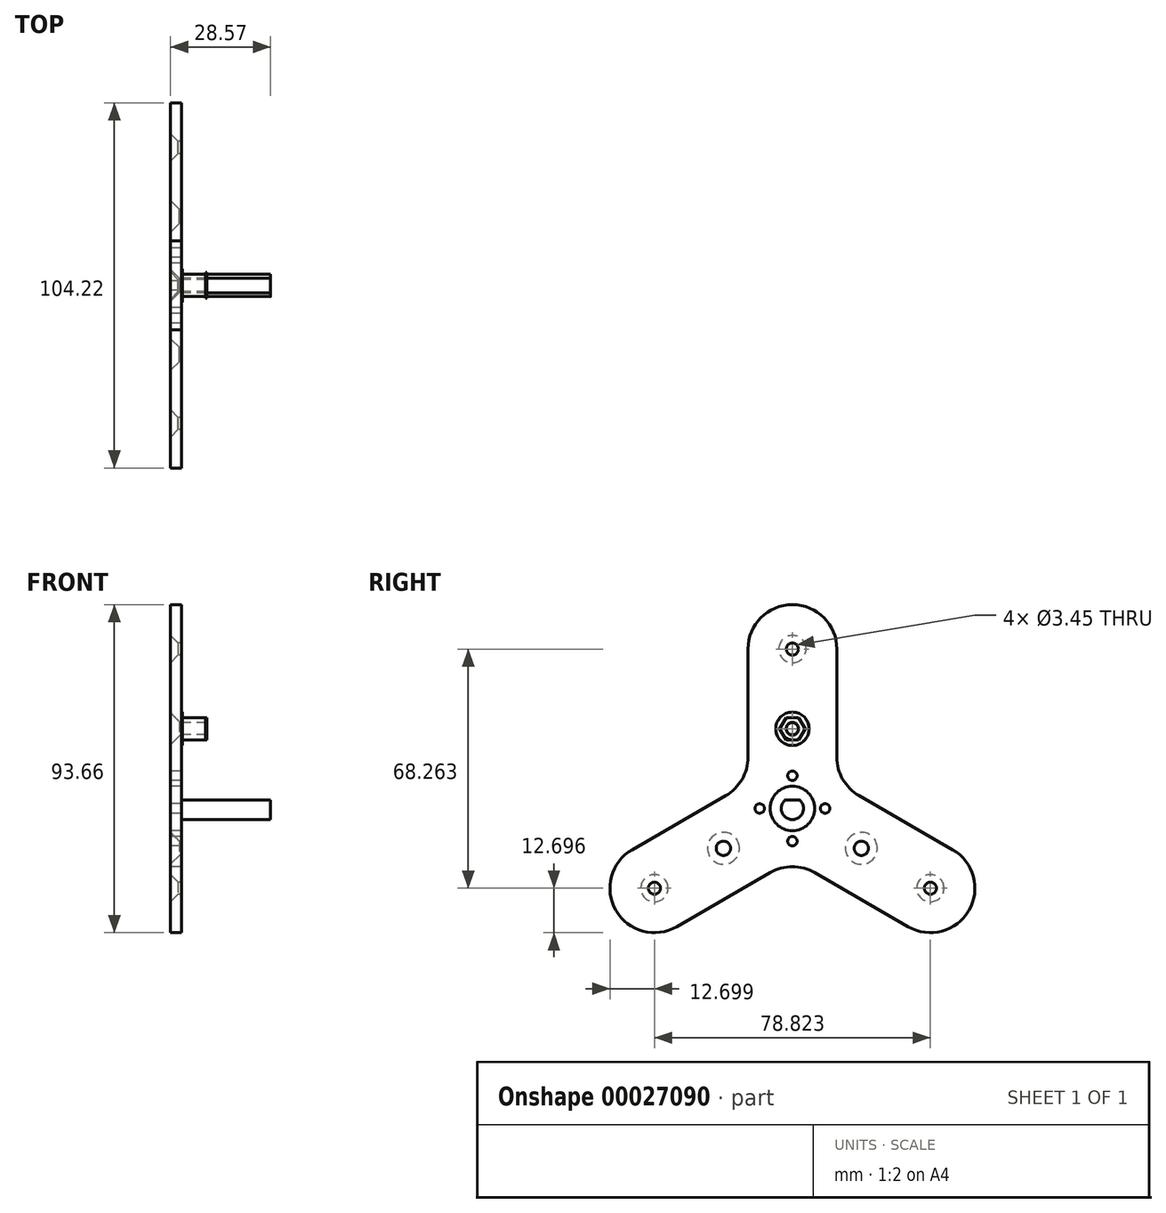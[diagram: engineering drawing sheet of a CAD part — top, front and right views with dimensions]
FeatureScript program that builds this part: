
annotation { "Feature Type Name" : "Feature", "Feature Type Description" : "" }
export const myFeature = defineFeature(function(context is Context, id is Id, definition is map)
    precondition{}
    {
        {
            var Q0;
            Q0=qCreatedBy(makeId("Right.planeOp"),FACE);
            var sketch = newSketch(context, id + "F0", { "sketchPlane" : qUnion([Q0])});
            skCircle(sketch, "E0.cCircle", {"center": v(0, 0) * mm, "radius": 45.5 * mm, "construction": true});
            skLineSegment(sketch, "E0.0", {"start": v(39.41, -22.75) * mm, "end": v(-39.41, -22.75) * mm, "construction": true});
            skLineSegment(sketch, "E0.2", {"start": v(0, 45.5) * mm, "end": v(39.41, -22.75) * mm, "construction": true});
            skCircle(sketch, "E1", {"center": v(-39.41, -22.75) * mm, "radius": 25.4 * mm});
            skCircle(sketch, "E2", {"center": v(39.41, -22.75) * mm, "radius": 25.4 * mm});
            skCircle(sketch, "E3", {"center": v(0, 45.5) * mm, "radius": 25.4 * mm});
            skCircle(sketch, "E4", {"center": v(0, 45.5) * mm, "radius": 14.82 * mm});
            skCircle(sketch, "E5", {"center": v(39.41, -22.75) * mm, "radius": 14.82 * mm});
            skCircle(sketch, "E6", {"center": v(-39.41, -22.75) * mm, "radius": 14.82 * mm});
            skCircle(sketch, "E7", {"center": v(0, 0) * mm, "radius": 14.82 * mm});
            skCircle(sketch, "E8", {"center": v(0, 22.75) * mm, "radius": 7.94 * mm});
            skCircle(sketch, "E9", {"center": v(19.7, -11.38) * mm, "radius": 7.94 * mm});
            skCircle(sketch, "E10", {"center": v(-19.7, -11.38) * mm, "radius": 7.94 * mm});
            skLineSegment(sketch, "E11", {"start": v(79.68, -48.15) * mm, "end": v(-88.84, -48.15) * mm, "construction": true});
            skCircle(sketch, "E12", {"center": v(0, 0) * mm, "radius": 12.7 * mm, "construction": true});
            skSolve(sketch);
        }
        {
            var Q0;
            Q0=qCreatedBy(makeId("Right.planeOp"),FACE);
            var sketch = newSketch(context, id + "F1", { "sketchPlane" : qUnion([Q0])});
            skPoint(sketch, "E13.0", {"position": v(0, 45.5) * mm});
            skPoint(sketch, "E13.1", {"position": v(39.41, -22.75) * mm});
            skPoint(sketch, "E13.2", {"position": v(-39.41, -22.75) * mm});
            skLineSegment(sketch, "E14", {"start": v(0, 45.5) * mm, "end": v(0, 0) * mm, "construction": true});
            skLineSegment(sketch, "E15", {"start": v(0, 0) * mm, "end": v(-39.41, -22.75) * mm, "construction": true});
            skLineSegment(sketch, "E16", {"start": v(0, 0) * mm, "end": v(39.41, -22.75) * mm, "construction": true});
            skArc(sketch, "E17.0.startCap", {"start": v(-6.35, -11) * mm, "mid": v(-11, 6.35) * mm, "end": v(6.35, 11) * mm, "construction": true});
            skArc(sketch, "E17.0.endCap", {"start": v(45.76, -11.76) * mm, "mid": v(50.4, -29.1) * mm, "end": v(33.06, -33.75) * mm});
            skLineSegment(sketch, "E17.0.left", {"start": v(19.05, 3.67) * mm, "end": v(45.76, -11.76) * mm});
            skLineSegment(sketch, "E17.0.right", {"start": v(6.35, -18.33) * mm, "end": v(33.06, -33.75) * mm});
            skArc(sketch, "E17.1.startCap", {"start": v(-6.35, 11) * mm, "mid": v(11, 6.35) * mm, "end": v(6.35, -11) * mm, "construction": true});
            skArc(sketch, "E17.1.endCap", {"start": v(-33.06, -33.75) * mm, "mid": v(-50.4, -29.1) * mm, "end": v(-45.76, -11.76) * mm});
            skLineSegment(sketch, "E17.1.left", {"start": v(-6.35, -18.33) * mm, "end": v(-33.06, -33.75) * mm});
            skLineSegment(sketch, "E17.1.right", {"start": v(-19.05, 3.67) * mm, "end": v(-45.76, -11.76) * mm});
            skArc(sketch, "E17.2.startCap", {"start": v(-12.7, 45.5) * mm, "mid": v(0, 58.2) * mm, "end": v(12.7, 45.5) * mm});
            skArc(sketch, "E17.2.endCap", {"start": v(12.7, 0) * mm, "mid": v(0, -12.7) * mm, "end": v(-12.7, 0) * mm, "construction": true});
            skLineSegment(sketch, "E17.2.left", {"start": v(12.7, 45.5) * mm, "end": v(12.7, 14.66) * mm});
            skLineSegment(sketch, "E17.2.right", {"start": v(-12.7, 45.5) * mm, "end": v(-12.7, 14.66) * mm});
            skPoint(sketch, "E18.0", {"position": v(0, 22.75) * mm});
            skPoint(sketch, "E18.1", {"position": v(19.7, -11.38) * mm});
            skPoint(sketch, "E18.2", {"position": v(-19.7, -11.38) * mm});
            skPoint(sketch, "E19.visualSharp", {"position": v(-12.7, 7.33) * mm});
            skArc(sketch, "E19.filletArc", {"start": v(-19.05, 3.67) * mm, "mid": v(-14.4, 8.31) * mm, "end": v(-12.7, 14.66) * mm});
            skPoint(sketch, "E20.visualSharp", {"position": v(0, -14.66) * mm});
            skArc(sketch, "E20.filletArc", {"start": v(6.35, -18.33) * mm, "mid": v(0, -16.63) * mm, "end": v(-6.35, -18.33) * mm});
            skPoint(sketch, "E21.visualSharp", {"position": v(12.7, 7.33) * mm});
            skArc(sketch, "E21.filletArc", {"start": v(12.7, 14.66) * mm, "mid": v(14.4, 8.31) * mm, "end": v(19.05, 3.67) * mm});
            skSolve(sketch);
        }
        {
            var Q0;
            Q0 = qSketchRegion(id + "F1", true);
            extrude(context, id + "F2", {"entities" : qUnion([Q0]), "depth" : 3.17 * mm});
        }
        {
            var Q0;
            Q0=sQuery(id+"F1.wireOp",VERTEX,"E13.0");
            var Q1;
            Q1=sQuery(id+"F1.wireOp",VERTEX,"E13.1");
            var Q2;
            Q2=sQuery(id+"F1.wireOp",VERTEX,"E13.2");
            var Q3;
            Q3=makeQuery(id+"F2.opExtrude","SWEPT_BODY",BODY,{"disambiguationData":[OSD([sQuery(id+"F1.wireOp",EDGE,"E17.0.endCap"),sQuery(id+"F1.wireOp",EDGE,"E17.0.left"),sQuery(id+"F1.wireOp",EDGE,"E17.0.right"),sQuery(id+"F1.wireOp",EDGE,"E17.1.endCap"),sQuery(id+"F1.wireOp",EDGE,"E17.1.left"),sQuery(id+"F1.wireOp",EDGE,"E17.1.right"),sQuery(id+"F1.wireOp",EDGE,"E17.2.startCap"),sQuery(id+"F1.wireOp",EDGE,"E17.2.left"),sQuery(id+"F1.wireOp",EDGE,"E17.2.right"),sQuery(id+"F1.wireOp",EDGE,"E19.filletArc"),sQuery(id+"F1.wireOp",EDGE,"E20.filletArc"),sQuery(id+"F1.wireOp",EDGE,"E21.filletArc")])]});
            hole(context, id + "F3", {"style" : HoleStyle.C_SINK, "holeDiameter" : 3.45 * mm, "cSinkDiameter" : 7.8 * mm, "endStyle" : HoleEndStyle.THROUGH, "oppositeDirection" : true, "locations" : qUnion([Q0, Q1, Q2]), "scope" : qUnion([Q3]), "cSinkAngle" : 90 * degree});
        }
        {
            var Q0;
            Q0=sQuery(id+"F1.wireOp",VERTEX,"E18.0");
            var Q1;
            Q1=sQuery(id+"F1.wireOp",VERTEX,"E18.2");
            var Q2;
            Q2=sQuery(id+"F1.wireOp",VERTEX,"E18.1");
            var Q3;
            Q3=makeQuery(id+"F2.opExtrude","SWEPT_BODY",BODY,{"disambiguationData":[OSD([sQuery(id+"F1.wireOp",EDGE,"E17.0.endCap"),sQuery(id+"F1.wireOp",EDGE,"E17.0.left"),sQuery(id+"F1.wireOp",EDGE,"E17.0.right"),sQuery(id+"F1.wireOp",EDGE,"E17.1.endCap"),sQuery(id+"F1.wireOp",EDGE,"E17.1.left"),sQuery(id+"F1.wireOp",EDGE,"E17.1.right"),sQuery(id+"F1.wireOp",EDGE,"E17.2.startCap"),sQuery(id+"F1.wireOp",EDGE,"E17.2.left"),sQuery(id+"F1.wireOp",EDGE,"E17.2.right"),sQuery(id+"F1.wireOp",EDGE,"E19.filletArc"),sQuery(id+"F1.wireOp",EDGE,"E20.filletArc"),sQuery(id+"F1.wireOp",EDGE,"E21.filletArc")])]});
            hole(context, id + "F4", {"style" : HoleStyle.SIMPLE, "holeDiameter" : 4.1 * mm, "endStyle" : HoleEndStyle.THROUGH, "oppositeDirection" : true, "locations" : qUnion([Q0, Q1, Q2]), "scope" : qUnion([Q3])});
        }
        {
            var Q0;
            Q0=makeQuery(id+"F2.opExtrude","CAP_FACE",FACE,{"disambiguationData":[OSD([sQuery(id+"F1.wireOp",EDGE,"E17.0.endCap"),sQuery(id+"F1.wireOp",EDGE,"E17.0.left"),sQuery(id+"F1.wireOp",EDGE,"E17.0.right"),sQuery(id+"F1.wireOp",EDGE,"E17.1.endCap"),sQuery(id+"F1.wireOp",EDGE,"E17.1.left"),sQuery(id+"F1.wireOp",EDGE,"E17.1.right"),sQuery(id+"F1.wireOp",EDGE,"E17.2.startCap"),sQuery(id+"F1.wireOp",EDGE,"E17.2.left"),sQuery(id+"F1.wireOp",EDGE,"E17.2.right"),sQuery(id+"F1.wireOp",EDGE,"E19.filletArc"),sQuery(id+"F1.wireOp",EDGE,"E20.filletArc"),sQuery(id+"F1.wireOp",EDGE,"E21.filletArc")])],"isStart":false});
            var sketch = newSketch(context, id + "F5", { "sketchPlane" : qUnion([Q0])});
            skCircle(sketch, "E22.cCircle", {"center": v(0, 22.75) * mm, "radius": 3.18 * mm});
            skLineSegment(sketch, "E22.0", {"start": v(3.67, 22.75) * mm, "end": v(1.83, 19.58) * mm});
            skLineSegment(sketch, "E22.1", {"start": v(1.83, 19.58) * mm, "end": v(-1.83, 19.58) * mm});
            skLineSegment(sketch, "E22.2", {"start": v(-1.83, 19.58) * mm, "end": v(-3.67, 22.75) * mm});
            skLineSegment(sketch, "E22.3", {"start": v(-3.67, 22.75) * mm, "end": v(-1.83, 25.93) * mm});
            skLineSegment(sketch, "E22.4", {"start": v(-1.83, 25.93) * mm, "end": v(1.83, 25.93) * mm});
            skLineSegment(sketch, "E22.5", {"start": v(1.83, 25.93) * mm, "end": v(3.67, 22.75) * mm});
            skPoint(sketch, "E22.0.midPoint", {"position": v(2.75, 21.17) * mm});
            skCircle(sketch, "E23", {"center": v(0, 22.75) * mm, "radius": 1.73 * mm});
            skCircle(sketch, "E24", {"center": v(0, 22.75) * mm, "radius": 4.76 * mm});
            skSolve(sketch);
        }
        {
            var Q0;
            {var subQ0=sQuery(id+"F5.wireOp",EDGE,"E22.cCircle");var subQ6=makeQuery(id+"F5.imprint","INTERSECT",VERTEX,{"derivedFrom":[subQ0,sQuery(id+"F5.wireOp",EDGE,"E22.4")]});Q0=makeQuery(id+"F5.imprint","IMPRINT",FACE,{"disambiguationData":[TD([[makeQuery(id+"F5.imprint","IMPRINT",EDGE,{"disambiguationData":[TD([[subQ6,1.0]])],"derivedFrom":subQ0}),1.0]])]});}
            var Q1;
            {var subQ0=sQuery(id+"F5.wireOp",EDGE,"E22.2");var subQ1=sQuery(id+"F5.wireOp",EDGE,"E22.cCircle");var subQ2=makeQuery(id+"F5.imprint","INTERSECT",VERTEX,{"derivedFrom":[subQ1,subQ0]});Q1=makeQuery(id+"F5.imprint","IMPRINT",FACE,{"disambiguationData":[TD([[makeQuery(id+"F5.imprint","IMPRINT",EDGE,{"disambiguationData":[TD([[subQ2,-1.0]])],"derivedFrom":subQ1}),-1.0]])]});}
            var Q2;
            {var subQ0=sQuery(id+"F5.wireOp",EDGE,"E22.3");var subQ1=sQuery(id+"F5.wireOp",EDGE,"E22.cCircle");var subQ2=makeQuery(id+"F5.imprint","INTERSECT",VERTEX,{"derivedFrom":[subQ1,subQ0]});Q2=makeQuery(id+"F5.imprint","IMPRINT",FACE,{"disambiguationData":[TD([[makeQuery(id+"F5.imprint","IMPRINT",EDGE,{"disambiguationData":[TD([[subQ2,-1.0]])],"derivedFrom":subQ1}),-1.0]])]});}
            var Q3;
            {var subQ0=sQuery(id+"F5.wireOp",EDGE,"E22.4");var subQ1=sQuery(id+"F5.wireOp",EDGE,"E22.cCircle");var subQ2=makeQuery(id+"F5.imprint","INTERSECT",VERTEX,{"derivedFrom":[subQ1,subQ0]});Q3=makeQuery(id+"F5.imprint","IMPRINT",FACE,{"disambiguationData":[TD([[makeQuery(id+"F5.imprint","IMPRINT",EDGE,{"disambiguationData":[TD([[subQ2,-1.0]])],"derivedFrom":subQ1}),-1.0]])]});}
            var Q4;
            {var subQ1=sQuery(id+"F5.wireOp",EDGE,"E22.cCircle");var subQ3=sQuery(id+"F5.wireOp",EDGE,"E22.4");var subQ5=makeQuery(id+"F5.imprint","INTERSECT",VERTEX,{"derivedFrom":[subQ1,subQ3]});Q4=makeQuery(id+"F5.imprint","IMPRINT",FACE,{"disambiguationData":[TD([[makeQuery(id+"F5.imprint","IMPRINT",EDGE,{"disambiguationData":[TD([[subQ5,1.0]])],"derivedFrom":subQ1}),-1.0]])]});}
            var Q5;
            {var subQ0=sQuery(id+"F5.wireOp",EDGE,"E22.5");var subQ1=sQuery(id+"F5.wireOp",EDGE,"E22.cCircle");var subQ2=makeQuery(id+"F5.imprint","INTERSECT",VERTEX,{"derivedFrom":[subQ1,subQ0]});Q5=makeQuery(id+"F5.imprint","IMPRINT",FACE,{"disambiguationData":[TD([[makeQuery(id+"F5.imprint","IMPRINT",EDGE,{"disambiguationData":[TD([[subQ2,1.0]])],"derivedFrom":subQ1}),-1.0]])]});}
            var Q6;
            {var subQ0=sQuery(id+"F5.wireOp",EDGE,"E22.1");var subQ1=sQuery(id+"F5.wireOp",EDGE,"E22.cCircle");var subQ2=makeQuery(id+"F5.imprint","INTERSECT",VERTEX,{"derivedFrom":[subQ1,subQ0]});Q6=makeQuery(id+"F5.imprint","IMPRINT",FACE,{"disambiguationData":[TD([[makeQuery(id+"F5.imprint","IMPRINT",EDGE,{"disambiguationData":[TD([[subQ2,-1.0]])],"derivedFrom":subQ1}),-1.0]])]});}
            var Q7;
            Q7=makeQuery(id+"F5.imprint","IMPRINT",FACE,{"disambiguationData":[TD([[makeQuery(id+"F5.imprint","IMPRINT",EDGE,{"derivedFrom":sQuery(id+"F5.wireOp",EDGE,"E23")}),-1.0]])]});
            extrude(context, id + "F6", {"entities" : qUnion([Q0, Q1, Q2, Q3, Q4, Q5, Q6, Q7]), "depth" : 7.24 * mm});
        }
        {
            var Q0;
            {var subQ1=sQuery(id+"F5.wireOp",EDGE,"E22.cCircle");var subQ3=sQuery(id+"F5.wireOp",EDGE,"E22.4");var subQ5=makeQuery(id+"F5.imprint","INTERSECT",VERTEX,{"derivedFrom":[subQ1,subQ3]});Q0=makeQuery(id+"F5.imprint","IMPRINT",FACE,{"disambiguationData":[TD([[makeQuery(id+"F5.imprint","IMPRINT",EDGE,{"disambiguationData":[TD([[subQ5,1.0]])],"derivedFrom":subQ1}),-1.0]])]});}
            var Q1;
            {var subQ0=sQuery(id+"F5.wireOp",EDGE,"E22.5");var subQ1=sQuery(id+"F5.wireOp",EDGE,"E22.cCircle");var subQ2=makeQuery(id+"F5.imprint","INTERSECT",VERTEX,{"derivedFrom":[subQ1,subQ0]});Q1=makeQuery(id+"F5.imprint","IMPRINT",FACE,{"disambiguationData":[TD([[makeQuery(id+"F5.imprint","IMPRINT",EDGE,{"disambiguationData":[TD([[subQ2,1.0]])],"derivedFrom":subQ1}),-1.0]])]});}
            var Q2;
            {var subQ0=sQuery(id+"F5.wireOp",EDGE,"E22.1");var subQ1=sQuery(id+"F5.wireOp",EDGE,"E22.cCircle");var subQ2=makeQuery(id+"F5.imprint","INTERSECT",VERTEX,{"derivedFrom":[subQ1,subQ0]});Q2=makeQuery(id+"F5.imprint","IMPRINT",FACE,{"disambiguationData":[TD([[makeQuery(id+"F5.imprint","IMPRINT",EDGE,{"disambiguationData":[TD([[subQ2,-1.0]])],"derivedFrom":subQ1}),-1.0]])]});}
            var Q3;
            {var subQ0=sQuery(id+"F5.wireOp",EDGE,"E22.3");var subQ1=sQuery(id+"F5.wireOp",EDGE,"E22.cCircle");var subQ2=makeQuery(id+"F5.imprint","INTERSECT",VERTEX,{"derivedFrom":[subQ1,subQ0]});Q3=makeQuery(id+"F5.imprint","IMPRINT",FACE,{"disambiguationData":[TD([[makeQuery(id+"F5.imprint","IMPRINT",EDGE,{"disambiguationData":[TD([[subQ2,-1.0]])],"derivedFrom":subQ1}),-1.0]])]});}
            var Q4;
            {var subQ0=sQuery(id+"F5.wireOp",EDGE,"E22.4");var subQ1=sQuery(id+"F5.wireOp",EDGE,"E22.cCircle");var subQ2=makeQuery(id+"F5.imprint","INTERSECT",VERTEX,{"derivedFrom":[subQ1,subQ0]});Q4=makeQuery(id+"F5.imprint","IMPRINT",FACE,{"disambiguationData":[TD([[makeQuery(id+"F5.imprint","IMPRINT",EDGE,{"disambiguationData":[TD([[subQ2,-1.0]])],"derivedFrom":subQ1}),-1.0]])]});}
            var Q5;
            {var subQ0=sQuery(id+"F5.wireOp",EDGE,"E22.2");var subQ1=sQuery(id+"F5.wireOp",EDGE,"E22.cCircle");var subQ2=makeQuery(id+"F5.imprint","INTERSECT",VERTEX,{"derivedFrom":[subQ1,subQ0]});Q5=makeQuery(id+"F5.imprint","IMPRINT",FACE,{"disambiguationData":[TD([[makeQuery(id+"F5.imprint","IMPRINT",EDGE,{"disambiguationData":[TD([[subQ2,-1.0]])],"derivedFrom":subQ1}),-1.0]])]});}
            extrude(context, id + "F7", {"entities" : qUnion([Q0, Q1, Q2, Q3, Q4, Q5]), "operationType" : NewBodyOperationType.REMOVE, "depth" : 6.8 * mm});
        }
        {
            var Q0;
            Q0=makeQuery(id+"F5.imprint","IMPRINT",FACE,{"disambiguationData":[TD([[makeQuery(id+"F5.imprint","IMPRINT",EDGE,{"derivedFrom":sQuery(id+"F5.wireOp",EDGE,"E24")}),1.0]])]});
            var Q1;
            {var subQ0=sQuery(id+"F5.wireOp",EDGE,"E22.4");var subQ1=sQuery(id+"F5.wireOp",EDGE,"E22.cCircle");var subQ2=makeQuery(id+"F5.imprint","INTERSECT",VERTEX,{"derivedFrom":[subQ1,subQ0]});Q1=makeQuery(id+"F5.imprint","IMPRINT",FACE,{"disambiguationData":[TD([[makeQuery(id+"F5.imprint","IMPRINT",EDGE,{"disambiguationData":[TD([[subQ2,-1.0]])],"derivedFrom":subQ1}),-1.0]])]});}
            var Q2;
            {var subQ0=sQuery(id+"F5.wireOp",EDGE,"E22.3");var subQ1=sQuery(id+"F5.wireOp",EDGE,"E22.cCircle");var subQ2=makeQuery(id+"F5.imprint","INTERSECT",VERTEX,{"derivedFrom":[subQ1,subQ0]});Q2=makeQuery(id+"F5.imprint","IMPRINT",FACE,{"disambiguationData":[TD([[makeQuery(id+"F5.imprint","IMPRINT",EDGE,{"disambiguationData":[TD([[subQ2,-1.0]])],"derivedFrom":subQ1}),-1.0]])]});}
            var Q3;
            {var subQ0=sQuery(id+"F5.wireOp",EDGE,"E22.2");var subQ1=sQuery(id+"F5.wireOp",EDGE,"E22.cCircle");var subQ2=makeQuery(id+"F5.imprint","INTERSECT",VERTEX,{"derivedFrom":[subQ1,subQ0]});Q3=makeQuery(id+"F5.imprint","IMPRINT",FACE,{"disambiguationData":[TD([[makeQuery(id+"F5.imprint","IMPRINT",EDGE,{"disambiguationData":[TD([[subQ2,-1.0]])],"derivedFrom":subQ1}),-1.0]])]});}
            var Q4;
            {var subQ0=sQuery(id+"F5.wireOp",EDGE,"E22.1");var subQ1=sQuery(id+"F5.wireOp",EDGE,"E22.cCircle");var subQ2=makeQuery(id+"F5.imprint","INTERSECT",VERTEX,{"derivedFrom":[subQ1,subQ0]});Q4=makeQuery(id+"F5.imprint","IMPRINT",FACE,{"disambiguationData":[TD([[makeQuery(id+"F5.imprint","IMPRINT",EDGE,{"disambiguationData":[TD([[subQ2,-1.0]])],"derivedFrom":subQ1}),-1.0]])]});}
            var Q5;
            {var subQ0=sQuery(id+"F5.wireOp",EDGE,"E22.5");var subQ1=sQuery(id+"F5.wireOp",EDGE,"E22.cCircle");var subQ2=makeQuery(id+"F5.imprint","INTERSECT",VERTEX,{"derivedFrom":[subQ1,subQ0]});Q5=makeQuery(id+"F5.imprint","IMPRINT",FACE,{"disambiguationData":[TD([[makeQuery(id+"F5.imprint","IMPRINT",EDGE,{"disambiguationData":[TD([[subQ2,1.0]])],"derivedFrom":subQ1}),-1.0]])]});}
            var Q6;
            {var subQ1=sQuery(id+"F5.wireOp",EDGE,"E22.cCircle");var subQ3=sQuery(id+"F5.wireOp",EDGE,"E22.4");var subQ5=makeQuery(id+"F5.imprint","INTERSECT",VERTEX,{"derivedFrom":[subQ1,subQ3]});Q6=makeQuery(id+"F5.imprint","IMPRINT",FACE,{"disambiguationData":[TD([[makeQuery(id+"F5.imprint","IMPRINT",EDGE,{"disambiguationData":[TD([[subQ5,1.0]])],"derivedFrom":subQ1}),-1.0]])]});}
            extrude(context, id + "F8", {"entities" : qUnion([Q0, Q1, Q2, Q3, Q4, Q5, Q6]), "depth" : 0.25 * mm});
        }
        {
            var Q0;
            Q0=sQuery(id+"F0.wireOp",VERTEX,"E8.center");
            var Q1;
            Q1=sQuery(id+"F0.wireOp",VERTEX,"E9.center");
            var Q2;
            Q2=sQuery(id+"F0.wireOp",VERTEX,"E10.center");
            var Q3;
            Q3=makeQuery(id+"F2.opExtrude","SWEPT_BODY",BODY,{"disambiguationData":[OSD([sQuery(id+"F1.wireOp",EDGE,"E17.0.endCap"),sQuery(id+"F1.wireOp",EDGE,"E17.0.left"),sQuery(id+"F1.wireOp",EDGE,"E17.0.right"),sQuery(id+"F1.wireOp",EDGE,"E17.1.endCap"),sQuery(id+"F1.wireOp",EDGE,"E17.1.left"),sQuery(id+"F1.wireOp",EDGE,"E17.1.right"),sQuery(id+"F1.wireOp",EDGE,"E17.2.startCap"),sQuery(id+"F1.wireOp",EDGE,"E17.2.left"),sQuery(id+"F1.wireOp",EDGE,"E17.2.right"),sQuery(id+"F1.wireOp",EDGE,"E19.filletArc"),sQuery(id+"F1.wireOp",EDGE,"E20.filletArc"),sQuery(id+"F1.wireOp",EDGE,"E21.filletArc")])]});
            hole(context, id + "F9", {"style" : HoleStyle.C_SINK, "holeDiameter" : 4.1 * mm, "cSinkDiameter" : 9.12 * mm, "endStyle" : HoleEndStyle.THROUGH, "oppositeDirection" : true, "locations" : qUnion([Q0, Q1, Q2]), "scope" : qUnion([Q3]), "cSinkAngle" : 90 * degree});
        }
        {
            var Q0;
            Q0=makeQuery(id+"F2.opExtrude","CAP_FACE",FACE,{"disambiguationData":[OSD([sQuery(id+"F1.wireOp",EDGE,"E17.0.endCap"),sQuery(id+"F1.wireOp",EDGE,"E17.0.left"),sQuery(id+"F1.wireOp",EDGE,"E17.0.right"),sQuery(id+"F1.wireOp",EDGE,"E17.1.endCap"),sQuery(id+"F1.wireOp",EDGE,"E17.1.left"),sQuery(id+"F1.wireOp",EDGE,"E17.1.right"),sQuery(id+"F1.wireOp",EDGE,"E17.2.startCap"),sQuery(id+"F1.wireOp",EDGE,"E17.2.left"),sQuery(id+"F1.wireOp",EDGE,"E17.2.right"),sQuery(id+"F1.wireOp",EDGE,"E19.filletArc"),sQuery(id+"F1.wireOp",EDGE,"E20.filletArc"),sQuery(id+"F1.wireOp",EDGE,"E21.filletArc")])],"isStart":true});
            var sketch = newSketch(context, id + "F10", { "sketchPlane" : qUnion([Q0])});
            skCircle(sketch, "E25", {"center": v(0, 0) * mm, "radius": 6.35 * mm});
            skCircle(sketch, "E26", {"center": v(0, 0) * mm, "radius": 6 * mm, "construction": true});
            skCircle(sketch, "E27", {"center": v(0, 0) * mm, "radius": 12.7 * mm, "construction": true});
            skLineSegment(sketch, "E28", {"start": v(0, 6) * mm, "end": v(0, 12.7) * mm, "construction": true});
            skCircle(sketch, "E29.cCircle", {"center": v(0, 0) * mm, "radius": 9.35 * mm, "construction": true});
            skLineSegment(sketch, "E29.0", {"start": v(0, 9.35) * mm, "end": v(9.35, 0) * mm, "construction": true});
            skLineSegment(sketch, "E29.1", {"start": v(9.35, 0) * mm, "end": v(0, -9.35) * mm, "construction": true});
            skLineSegment(sketch, "E29.2", {"start": v(0, -9.35) * mm, "end": v(-9.35, 0) * mm, "construction": true});
            skLineSegment(sketch, "E29.3", {"start": v(-9.35, 0) * mm, "end": v(0, 9.35) * mm, "construction": true});
            skSolve(sketch);
        }
        {
            var Q0;
            Q0 = qSketchRegion(id + "F10", true);
            extrude(context, id + "F11", {"entities" : qUnion([Q0]), "operationType" : NewBodyOperationType.REMOVE, "endBound" : BoundingType.UP_TO_NEXT, "oppositeDirection" : true, "depth" : 25.4 * mm});
        }
        {
            var Q0;
            Q0=sQuery(id+"F10.wireOp",VERTEX,"E29.3.end");
            var Q1;
            Q1=sQuery(id+"F10.wireOp",VERTEX,"E29.2.end");
            var Q2;
            Q2=sQuery(id+"F10.wireOp",VERTEX,"E29.1.end");
            var Q3;
            Q3=sQuery(id+"F10.wireOp",VERTEX,"E29.0.end");
            var Q4;
            Q4=makeQuery(id+"F2.opExtrude","SWEPT_BODY",BODY,{"disambiguationData":[OSD([sQuery(id+"F1.wireOp",EDGE,"E17.0.endCap"),sQuery(id+"F1.wireOp",EDGE,"E17.0.left"),sQuery(id+"F1.wireOp",EDGE,"E17.0.right"),sQuery(id+"F1.wireOp",EDGE,"E17.1.endCap"),sQuery(id+"F1.wireOp",EDGE,"E17.1.left"),sQuery(id+"F1.wireOp",EDGE,"E17.1.right"),sQuery(id+"F1.wireOp",EDGE,"E17.2.startCap"),sQuery(id+"F1.wireOp",EDGE,"E17.2.left"),sQuery(id+"F1.wireOp",EDGE,"E17.2.right"),sQuery(id+"F1.wireOp",EDGE,"E19.filletArc"),sQuery(id+"F1.wireOp",EDGE,"E20.filletArc"),sQuery(id+"F1.wireOp",EDGE,"E21.filletArc")])]});
            hole(context, id + "F12", {"style" : HoleStyle.SIMPLE, "holeDiameter" : 2.7 * mm, "endStyle" : HoleEndStyle.THROUGH, "locations" : qUnion([Q0, Q1, Q2, Q3]), "scope" : qUnion([Q4])});
        }
        {
            var Q0;
            Q0=makeQuery(id+"F2.opExtrude","CAP_FACE",FACE,{"disambiguationData":[OSD([sQuery(id+"F1.wireOp",EDGE,"E17.0.endCap"),sQuery(id+"F1.wireOp",EDGE,"E17.0.left"),sQuery(id+"F1.wireOp",EDGE,"E17.0.right"),sQuery(id+"F1.wireOp",EDGE,"E17.1.endCap"),sQuery(id+"F1.wireOp",EDGE,"E17.1.left"),sQuery(id+"F1.wireOp",EDGE,"E17.1.right"),sQuery(id+"F1.wireOp",EDGE,"E17.2.startCap"),sQuery(id+"F1.wireOp",EDGE,"E17.2.left"),sQuery(id+"F1.wireOp",EDGE,"E17.2.right"),sQuery(id+"F1.wireOp",EDGE,"E19.filletArc"),sQuery(id+"F1.wireOp",EDGE,"E20.filletArc"),sQuery(id+"F1.wireOp",EDGE,"E21.filletArc")])],"isStart":false});
            var sketch = newSketch(context, id + "F13", { "sketchPlane" : qUnion([Q0])});
            skArc(sketch, "E30", {"start": v(-2.07, 2.41) * mm, "mid": v(0, -3.17) * mm, "end": v(2.07, 2.41) * mm});
            skLineSegment(sketch, "E31", {"start": v(2.07, 2.41) * mm, "end": v(-2.07, 2.41) * mm});
            skSolve(sketch);
        }
        {
            var Q0;
            Q0 = qSketchRegion(id + "F13", true);
            extrude(context, id + "F14", {"entities" : qUnion([Q0]), "depth" : 25.4 * mm});
        }
    });
